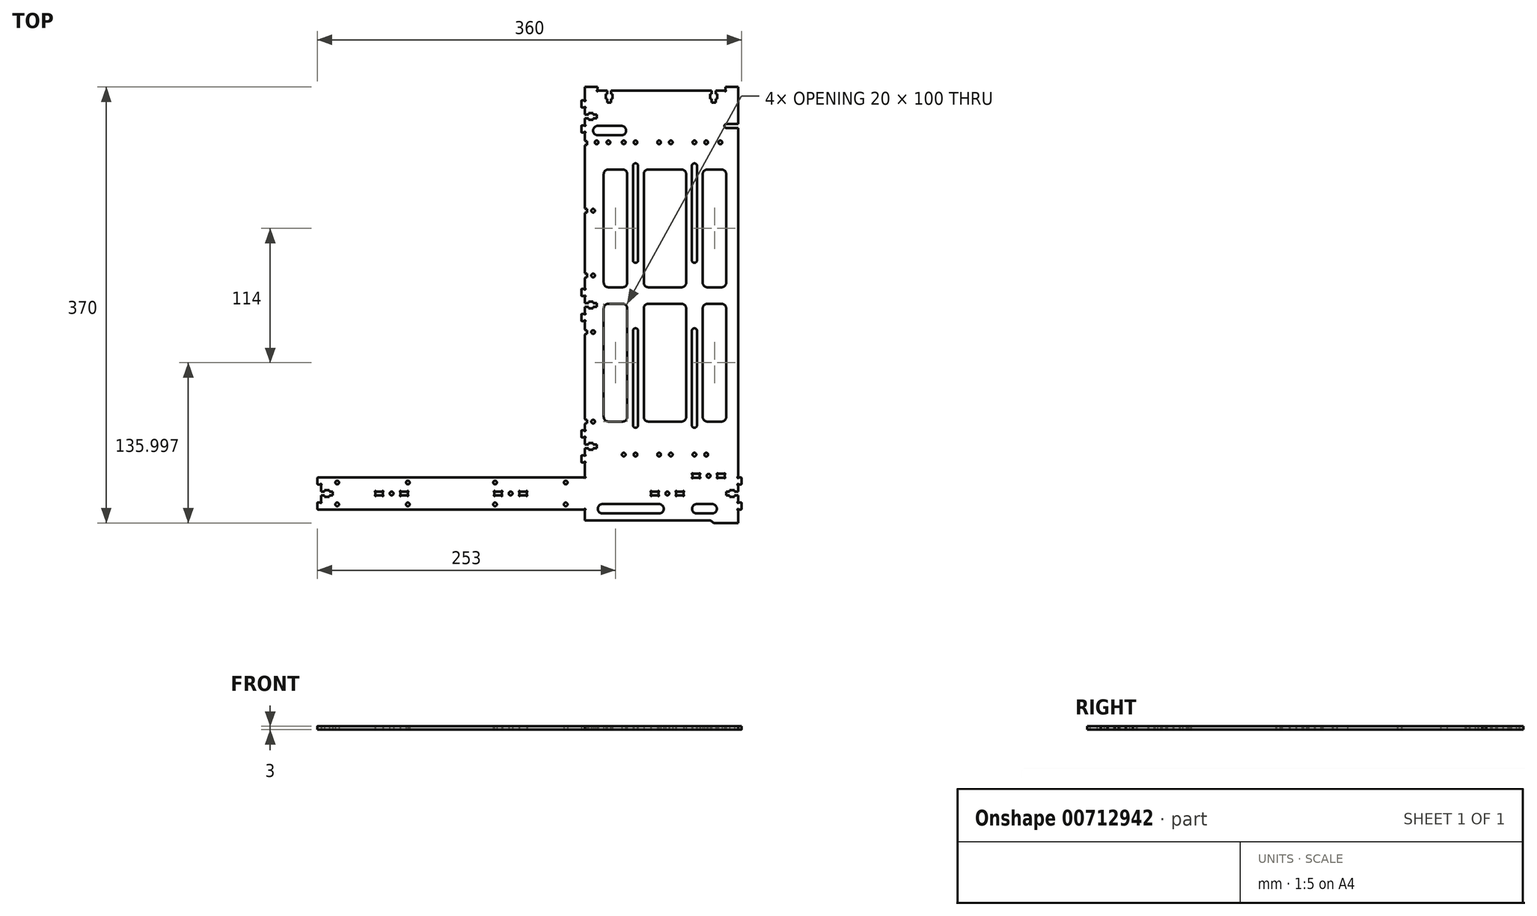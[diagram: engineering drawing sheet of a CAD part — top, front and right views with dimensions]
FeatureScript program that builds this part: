
annotation { "Feature Type Name" : "Feature", "Feature Type Description" : "" }
export const myFeature = defineFeature(function(context is Context, id is Id, definition is map)
    precondition{}
    {
        {
            var Q0;
            Q0=qCreatedBy(makeId("Top.planeOp"),FACE);
            var sketch = newSketch(context, id + "F0", { "sketchPlane" : qUnion([Q0])});
            skCircle(sketch, "E0", {"center": v(30.75, -146.86) * mm, "radius": 1.55 * mm});
            skCircle(sketch, "E1", {"center": v(-103.25, -146.86) * mm, "radius": 1.55 * mm});
            skCircle(sketch, "E2", {"center": v(30.75, -165.45) * mm, "radius": 1.55 * mm});
            skCircle(sketch, "E3", {"center": v(-163.25, -165.45) * mm, "radius": 1.55 * mm});
            skLineSegment(sketch, "E4", {"start": v(-103.3, -156.94) * mm, "end": v(-103.3, -155.37) * mm});
            skArc(sketch, "E5", {"start": v(-103.3, -156.94) * mm, "mid": v(-103.23, -157.19) * mm, "end": v(-103.05, -157.37) * mm});
            skArc(sketch, "E6", {"start": v(-103.73, -158.05) * mm, "mid": v(-102.95, -158.16) * mm, "end": v(-103.05, -157.37) * mm});
            skArc(sketch, "E7", {"start": v(-103.73, -158.05) * mm, "mid": v(-103.92, -157.87) * mm, "end": v(-104.17, -157.8) * mm});
            skLineSegment(sketch, "E8", {"start": v(-108.63, -157.8) * mm, "end": v(-104.17, -157.8) * mm});
            skArc(sketch, "E9", {"start": v(-108.63, -157.8) * mm, "mid": v(-108.88, -157.87) * mm, "end": v(-109.07, -158.05) * mm});
            skArc(sketch, "E10", {"start": v(-109.75, -157.37) * mm, "mid": v(-109.85, -158.16) * mm, "end": v(-109.07, -158.05) * mm});
            skArc(sketch, "E11", {"start": v(-109.75, -157.37) * mm, "mid": v(-109.57, -157.19) * mm, "end": v(-109.5, -156.94) * mm});
            skLineSegment(sketch, "E12", {"start": v(-109.5, -155.37) * mm, "end": v(-109.5, -156.94) * mm});
            skArc(sketch, "E13", {"start": v(-109.5, -155.37) * mm, "mid": v(-109.57, -155.12) * mm, "end": v(-109.75, -154.94) * mm});
            skArc(sketch, "E14", {"start": v(-109.07, -154.25) * mm, "mid": v(-109.85, -154.15) * mm, "end": v(-109.75, -154.94) * mm});
            skArc(sketch, "E15", {"start": v(-109.07, -154.25) * mm, "mid": v(-108.88, -154.44) * mm, "end": v(-108.63, -154.5) * mm});
            skLineSegment(sketch, "E16", {"start": v(-104.17, -154.5) * mm, "end": v(-108.63, -154.5) * mm});
            skArc(sketch, "E17", {"start": v(-104.17, -154.5) * mm, "mid": v(-103.92, -154.44) * mm, "end": v(-103.73, -154.25) * mm});
            skArc(sketch, "E18", {"start": v(-103.05, -154.94) * mm, "mid": v(-102.95, -154.15) * mm, "end": v(-103.73, -154.25) * mm});
            skArc(sketch, "E19", {"start": v(-103.05, -154.94) * mm, "mid": v(-103.23, -155.12) * mm, "end": v(-103.3, -155.37) * mm});
            skLineSegment(sketch, "E20", {"start": v(-124.5, -156.94) * mm, "end": v(-124.5, -155.37) * mm});
            skArc(sketch, "E21", {"start": v(-124.5, -156.94) * mm, "mid": v(-124.43, -157.19) * mm, "end": v(-124.25, -157.37) * mm});
            skArc(sketch, "E22", {"start": v(-124.93, -158.05) * mm, "mid": v(-124.15, -158.16) * mm, "end": v(-124.25, -157.37) * mm});
            skArc(sketch, "E23", {"start": v(-124.93, -158.05) * mm, "mid": v(-125.12, -157.87) * mm, "end": v(-125.37, -157.8) * mm});
            skLineSegment(sketch, "E24", {"start": v(-129.83, -157.8) * mm, "end": v(-125.37, -157.8) * mm});
            skArc(sketch, "E25", {"start": v(-129.83, -157.8) * mm, "mid": v(-130.08, -157.87) * mm, "end": v(-130.27, -158.05) * mm});
            skArc(sketch, "E26", {"start": v(-130.95, -157.37) * mm, "mid": v(-131.05, -158.16) * mm, "end": v(-130.27, -158.05) * mm});
            skArc(sketch, "E27", {"start": v(-130.95, -157.37) * mm, "mid": v(-130.77, -157.19) * mm, "end": v(-130.7, -156.94) * mm});
            skLineSegment(sketch, "E28", {"start": v(-130.7, -155.37) * mm, "end": v(-130.7, -156.94) * mm});
            skArc(sketch, "E29", {"start": v(-130.7, -155.37) * mm, "mid": v(-130.77, -155.12) * mm, "end": v(-130.95, -154.94) * mm});
            skArc(sketch, "E30", {"start": v(-130.27, -154.25) * mm, "mid": v(-131.05, -154.15) * mm, "end": v(-130.95, -154.94) * mm});
            skArc(sketch, "E31", {"start": v(-130.27, -154.25) * mm, "mid": v(-130.08, -154.44) * mm, "end": v(-129.83, -154.5) * mm});
            skLineSegment(sketch, "E32", {"start": v(-125.37, -154.5) * mm, "end": v(-129.83, -154.5) * mm});
            skArc(sketch, "E33", {"start": v(-125.37, -154.5) * mm, "mid": v(-125.12, -154.44) * mm, "end": v(-124.93, -154.25) * mm});
            skArc(sketch, "E34", {"start": v(-124.25, -154.94) * mm, "mid": v(-124.15, -154.15) * mm, "end": v(-124.93, -154.25) * mm});
            skArc(sketch, "E35", {"start": v(-124.25, -154.94) * mm, "mid": v(-124.43, -155.12) * mm, "end": v(-124.5, -155.37) * mm});
            skLineSegment(sketch, "E36", {"start": v(87.8, -18.15) * mm, "end": v(87.8, -98.15) * mm});
            skArc(sketch, "E37", {"start": v(92.2, -18.15) * mm, "mid": v(90, -15.95) * mm, "end": v(87.8, -18.15) * mm});
            skLineSegment(sketch, "E38", {"start": v(92.2, -98.15) * mm, "end": v(92.2, -18.15) * mm});
            skArc(sketch, "E39", {"start": v(87.8, -98.15) * mm, "mid": v(90, -100.35) * mm, "end": v(92.2, -98.15) * mm});
            skLineSegment(sketch, "E40", {"start": v(137.8, -18.15) * mm, "end": v(137.8, -98.15) * mm});
            skArc(sketch, "E41", {"start": v(142.2, -18.15) * mm, "mid": v(140, -15.95) * mm, "end": v(137.8, -18.15) * mm});
            skLineSegment(sketch, "E42", {"start": v(142.2, -98.15) * mm, "end": v(142.2, -18.15) * mm});
            skArc(sketch, "E43", {"start": v(137.8, -98.15) * mm, "mid": v(140, -100.35) * mm, "end": v(142.2, -98.15) * mm});
            skCircle(sketch, "E44", {"center": v(162, 141.85) * mm, "radius": 1.55 * mm});
            skCircle(sketch, "E45", {"center": v(140, 141.85) * mm, "radius": 1.55 * mm});
            skCircle(sketch, "E46", {"center": v(110, 141.85) * mm, "radius": 1.55 * mm});
            skCircle(sketch, "E47", {"center": v(80, 141.85) * mm, "radius": 1.55 * mm});
            skCircle(sketch, "E48", {"center": v(57, 141.85) * mm, "radius": 1.55 * mm});
            skLineSegment(sketch, "E49", {"start": v(165.7, -141.94) * mm, "end": v(165.7, -140.37) * mm});
            skArc(sketch, "E50", {"start": v(165.7, -141.94) * mm, "mid": v(165.77, -142.19) * mm, "end": v(165.95, -142.37) * mm});
            skArc(sketch, "E51", {"start": v(165.27, -143.05) * mm, "mid": v(166.05, -143.16) * mm, "end": v(165.95, -142.37) * mm});
            skArc(sketch, "E52", {"start": v(165.27, -143.05) * mm, "mid": v(165.08, -142.87) * mm, "end": v(164.83, -142.8) * mm});
            skLineSegment(sketch, "E53", {"start": v(160.37, -142.8) * mm, "end": v(164.83, -142.8) * mm});
            skArc(sketch, "E54", {"start": v(160.37, -142.8) * mm, "mid": v(160.12, -142.87) * mm, "end": v(159.93, -143.05) * mm});
            skArc(sketch, "E55", {"start": v(159.25, -142.37) * mm, "mid": v(159.15, -143.16) * mm, "end": v(159.93, -143.05) * mm});
            skArc(sketch, "E56", {"start": v(159.25, -142.37) * mm, "mid": v(159.43, -142.19) * mm, "end": v(159.5, -141.94) * mm});
            skLineSegment(sketch, "E57", {"start": v(159.5, -140.37) * mm, "end": v(159.5, -141.94) * mm});
            skArc(sketch, "E58", {"start": v(159.5, -140.37) * mm, "mid": v(159.43, -140.12) * mm, "end": v(159.25, -139.94) * mm});
            skArc(sketch, "E59", {"start": v(159.93, -139.25) * mm, "mid": v(159.15, -139.15) * mm, "end": v(159.25, -139.94) * mm});
            skArc(sketch, "E60", {"start": v(159.93, -139.25) * mm, "mid": v(160.12, -139.44) * mm, "end": v(160.37, -139.5) * mm});
            skLineSegment(sketch, "E61", {"start": v(164.83, -139.5) * mm, "end": v(160.37, -139.5) * mm});
            skArc(sketch, "E62", {"start": v(164.83, -139.5) * mm, "mid": v(165.08, -139.44) * mm, "end": v(165.27, -139.25) * mm});
            skArc(sketch, "E63", {"start": v(165.95, -139.94) * mm, "mid": v(166.05, -139.15) * mm, "end": v(165.27, -139.25) * mm});
            skArc(sketch, "E64", {"start": v(165.95, -139.94) * mm, "mid": v(165.77, -140.12) * mm, "end": v(165.7, -140.37) * mm});
            skLineSegment(sketch, "E65", {"start": v(144.5, -141.94) * mm, "end": v(144.5, -140.37) * mm});
            skArc(sketch, "E66", {"start": v(144.5, -141.94) * mm, "mid": v(144.57, -142.19) * mm, "end": v(144.75, -142.37) * mm});
            skArc(sketch, "E67", {"start": v(144.07, -143.05) * mm, "mid": v(144.85, -143.16) * mm, "end": v(144.75, -142.37) * mm});
            skArc(sketch, "E68", {"start": v(144.07, -143.05) * mm, "mid": v(143.88, -142.87) * mm, "end": v(143.63, -142.8) * mm});
            skLineSegment(sketch, "E69", {"start": v(139.17, -142.8) * mm, "end": v(143.63, -142.8) * mm});
            skArc(sketch, "E70", {"start": v(139.17, -142.8) * mm, "mid": v(138.92, -142.87) * mm, "end": v(138.73, -143.05) * mm});
            skArc(sketch, "E71", {"start": v(138.05, -142.37) * mm, "mid": v(137.95, -143.16) * mm, "end": v(138.73, -143.05) * mm});
            skArc(sketch, "E72", {"start": v(138.05, -142.37) * mm, "mid": v(138.23, -142.19) * mm, "end": v(138.3, -141.94) * mm});
            skLineSegment(sketch, "E73", {"start": v(138.3, -140.37) * mm, "end": v(138.3, -141.94) * mm});
            skArc(sketch, "E74", {"start": v(138.3, -140.37) * mm, "mid": v(138.23, -140.12) * mm, "end": v(138.05, -139.94) * mm});
            skArc(sketch, "E75", {"start": v(138.73, -139.25) * mm, "mid": v(137.95, -139.15) * mm, "end": v(138.05, -139.94) * mm});
            skArc(sketch, "E76", {"start": v(138.73, -139.25) * mm, "mid": v(138.92, -139.44) * mm, "end": v(139.17, -139.5) * mm});
            skLineSegment(sketch, "E77", {"start": v(143.63, -139.5) * mm, "end": v(139.17, -139.5) * mm});
            skArc(sketch, "E78", {"start": v(143.63, -139.5) * mm, "mid": v(143.88, -139.44) * mm, "end": v(144.07, -139.25) * mm});
            skArc(sketch, "E79", {"start": v(144.75, -139.94) * mm, "mid": v(144.85, -139.15) * mm, "end": v(144.07, -139.25) * mm});
            skArc(sketch, "E80", {"start": v(144.75, -139.94) * mm, "mid": v(144.57, -140.12) * mm, "end": v(144.5, -140.37) * mm});
            skCircle(sketch, "E81", {"center": v(117, -156.15) * mm, "radius": 1.6 * mm});
            skCircle(sketch, "E82", {"center": v(80, -123.15) * mm, "radius": 1.55 * mm});
            skCircle(sketch, "E83", {"center": v(140, -123.15) * mm, "radius": 1.55 * mm});
            skCircle(sketch, "E84", {"center": v(110, -123.15) * mm, "radius": 1.55 * mm});
            skCircle(sketch, "E85", {"center": v(54, -95.15) * mm, "radius": 1.55 * mm});
            skCircle(sketch, "E86", {"center": v(54, 28.85) * mm, "radius": 1.55 * mm});
            skLineSegment(sketch, "E87", {"start": v(-2.3, -156.94) * mm, "end": v(-2.3, -155.37) * mm});
            skArc(sketch, "E88", {"start": v(-2.3, -156.94) * mm, "mid": v(-2.23, -157.19) * mm, "end": v(-2.05, -157.37) * mm});
            skArc(sketch, "E89", {"start": v(-2.73, -158.05) * mm, "mid": v(-1.95, -158.16) * mm, "end": v(-2.05, -157.37) * mm});
            skArc(sketch, "E90", {"start": v(-2.73, -158.05) * mm, "mid": v(-2.92, -157.87) * mm, "end": v(-3.17, -157.8) * mm});
            skLineSegment(sketch, "E91", {"start": v(-7.63, -157.8) * mm, "end": v(-3.17, -157.8) * mm});
            skArc(sketch, "E92", {"start": v(-7.63, -157.8) * mm, "mid": v(-7.88, -157.87) * mm, "end": v(-8.07, -158.05) * mm});
            skArc(sketch, "E93", {"start": v(-8.75, -157.37) * mm, "mid": v(-8.85, -158.16) * mm, "end": v(-8.07, -158.05) * mm});
            skArc(sketch, "E94", {"start": v(-8.75, -157.37) * mm, "mid": v(-8.57, -157.19) * mm, "end": v(-8.5, -156.94) * mm});
            skLineSegment(sketch, "E95", {"start": v(-8.5, -155.37) * mm, "end": v(-8.5, -156.94) * mm});
            skArc(sketch, "E96", {"start": v(-8.5, -155.37) * mm, "mid": v(-8.57, -155.12) * mm, "end": v(-8.75, -154.94) * mm});
            skArc(sketch, "E97", {"start": v(-8.07, -154.25) * mm, "mid": v(-8.85, -154.15) * mm, "end": v(-8.75, -154.94) * mm});
            skArc(sketch, "E98", {"start": v(-8.07, -154.25) * mm, "mid": v(-7.88, -154.44) * mm, "end": v(-7.63, -154.5) * mm});
            skLineSegment(sketch, "E99", {"start": v(-3.17, -154.5) * mm, "end": v(-7.63, -154.5) * mm});
            skArc(sketch, "E100", {"start": v(-3.17, -154.5) * mm, "mid": v(-2.92, -154.44) * mm, "end": v(-2.73, -154.25) * mm});
            skArc(sketch, "E101", {"start": v(-2.05, -154.94) * mm, "mid": v(-1.95, -154.15) * mm, "end": v(-2.73, -154.25) * mm});
            skArc(sketch, "E102", {"start": v(-2.05, -154.94) * mm, "mid": v(-2.23, -155.12) * mm, "end": v(-2.3, -155.37) * mm});
            skLineSegment(sketch, "E103", {"start": v(-23.5, -156.94) * mm, "end": v(-23.5, -155.37) * mm});
            skArc(sketch, "E104", {"start": v(-23.5, -156.94) * mm, "mid": v(-23.43, -157.19) * mm, "end": v(-23.25, -157.37) * mm});
            skArc(sketch, "E105", {"start": v(-23.93, -158.05) * mm, "mid": v(-23.15, -158.16) * mm, "end": v(-23.25, -157.37) * mm});
            skArc(sketch, "E106", {"start": v(-23.93, -158.05) * mm, "mid": v(-24.12, -157.87) * mm, "end": v(-24.37, -157.8) * mm});
            skLineSegment(sketch, "E107", {"start": v(-28.83, -157.8) * mm, "end": v(-24.37, -157.8) * mm});
            skArc(sketch, "E108", {"start": v(-28.83, -157.8) * mm, "mid": v(-29.08, -157.87) * mm, "end": v(-29.27, -158.05) * mm});
            skArc(sketch, "E109", {"start": v(-29.95, -157.37) * mm, "mid": v(-30.05, -158.16) * mm, "end": v(-29.27, -158.05) * mm});
            skArc(sketch, "E110", {"start": v(-29.95, -157.37) * mm, "mid": v(-29.77, -157.19) * mm, "end": v(-29.7, -156.94) * mm});
            skLineSegment(sketch, "E111", {"start": v(-29.7, -155.37) * mm, "end": v(-29.7, -156.94) * mm});
            skArc(sketch, "E112", {"start": v(-29.7, -155.37) * mm, "mid": v(-29.77, -155.12) * mm, "end": v(-29.95, -154.94) * mm});
            skArc(sketch, "E113", {"start": v(-29.27, -154.25) * mm, "mid": v(-30.05, -154.15) * mm, "end": v(-29.95, -154.94) * mm});
            skArc(sketch, "E114", {"start": v(-29.27, -154.25) * mm, "mid": v(-29.08, -154.44) * mm, "end": v(-28.83, -154.5) * mm});
            skLineSegment(sketch, "E115", {"start": v(-24.37, -154.5) * mm, "end": v(-28.83, -154.5) * mm});
            skArc(sketch, "E116", {"start": v(-24.37, -154.5) * mm, "mid": v(-24.12, -154.44) * mm, "end": v(-23.93, -154.25) * mm});
            skArc(sketch, "E117", {"start": v(-23.25, -154.94) * mm, "mid": v(-23.15, -154.15) * mm, "end": v(-23.93, -154.25) * mm});
            skArc(sketch, "E118", {"start": v(-23.25, -154.94) * mm, "mid": v(-23.43, -155.12) * mm, "end": v(-23.5, -155.37) * mm});
            skLineSegment(sketch, "E119", {"start": v(62, -173.15) * mm, "end": v(110, -173.15) * mm});
            skArc(sketch, "E120", {"start": v(62, -165.15) * mm, "mid": v(58, -169.15) * mm, "end": v(62, -173.15) * mm});
            skLineSegment(sketch, "E121", {"start": v(110, -165.15) * mm, "end": v(62, -165.15) * mm});
            skArc(sketch, "E122", {"start": v(110, -173.15) * mm, "mid": v(114, -169.15) * mm, "end": v(110, -165.15) * mm});
            skArc(sketch, "E123", {"start": v(47.25, -170.19) * mm, "mid": v(47.35, -169.4) * mm, "end": v(46.57, -169.5) * mm});
            skArc(sketch, "E124", {"start": v(47.25, -170.19) * mm, "mid": v(47.07, -170.37) * mm, "end": v(47, -170.62) * mm});
            skLineSegment(sketch, "E125", {"start": v(47, -170.62) * mm, "end": v(47, -179.15) * mm});
            skLineSegment(sketch, "E126", {"start": v(47, -179.15) * mm, "end": v(153.17, -179.15) * mm});
            skArc(sketch, "E127", {"start": v(154.59, -179.74) * mm, "mid": v(153.94, -179.3) * mm, "end": v(153.17, -179.15) * mm});
            skLineSegment(sketch, "E128", {"start": v(154.59, -179.74) * mm, "end": v(155.41, -180.57) * mm});
            skArc(sketch, "E129", {"start": v(155.41, -180.57) * mm, "mid": v(156.06, -181) * mm, "end": v(156.83, -181.15) * mm});
            skLineSegment(sketch, "E130", {"start": v(156.83, -181.15) * mm, "end": v(177, -181.15) * mm});
            skLineSegment(sketch, "E131", {"start": v(177, -181.15) * mm, "end": v(177, -170.62) * mm});
            skArc(sketch, "E132", {"start": v(177, -170.62) * mm, "mid": v(176.93, -170.37) * mm, "end": v(176.75, -170.19) * mm});
            skArc(sketch, "E133", {"start": v(177.43, -169.5) * mm, "mid": v(176.65, -169.4) * mm, "end": v(176.75, -170.19) * mm});
            skArc(sketch, "E134", {"start": v(177.43, -169.5) * mm, "mid": v(177.62, -169.69) * mm, "end": v(177.87, -169.75) * mm});
            skLineSegment(sketch, "E135", {"start": v(177.87, -169.75) * mm, "end": v(179.5, -169.75) * mm});
            skArc(sketch, "E136", {"start": v(179.5, -169.75) * mm, "mid": v(179.85, -169.6) * mm, "end": v(180, -169.25) * mm});
            skLineSegment(sketch, "E137", {"start": v(180, -169.25) * mm, "end": v(180, -164.25) * mm});
            skArc(sketch, "E138", {"start": v(180, -164.25) * mm, "mid": v(179.85, -163.9) * mm, "end": v(179.5, -163.75) * mm});
            skLineSegment(sketch, "E139", {"start": v(179.5, -163.75) * mm, "end": v(177.87, -163.75) * mm});
            skArc(sketch, "E140", {"start": v(177.87, -163.75) * mm, "mid": v(177.62, -163.82) * mm, "end": v(177.43, -164) * mm});
            skArc(sketch, "E141", {"start": v(176.75, -163.32) * mm, "mid": v(176.65, -164.1) * mm, "end": v(177.43, -164) * mm});
            skArc(sketch, "E142", {"start": v(176.75, -163.32) * mm, "mid": v(176.93, -163.14) * mm, "end": v(177, -162.89) * mm});
            skLineSegment(sketch, "E143", {"start": v(177, -162.89) * mm, "end": v(177, -157.75) * mm});
            skLineSegment(sketch, "E144", {"start": v(177, -157.75) * mm, "end": v(174, -157.75) * mm});
            skLineSegment(sketch, "E145", {"start": v(174, -157.75) * mm, "end": v(174, -159.03) * mm});
            skLineSegment(sketch, "E146", {"start": v(174, -159.03) * mm, "end": v(170, -159.03) * mm});
            skLineSegment(sketch, "E147", {"start": v(170, -159.03) * mm, "end": v(170, -157.75) * mm});
            skLineSegment(sketch, "E148", {"start": v(170, -157.75) * mm, "end": v(167, -157.75) * mm});
            skLineSegment(sketch, "E149", {"start": v(167, -157.75) * mm, "end": v(167, -154.55) * mm});
            skLineSegment(sketch, "E150", {"start": v(167, -154.55) * mm, "end": v(170, -154.55) * mm});
            skLineSegment(sketch, "E151", {"start": v(170, -154.55) * mm, "end": v(170, -153.28) * mm});
            skLineSegment(sketch, "E152", {"start": v(170, -153.28) * mm, "end": v(174, -153.28) * mm});
            skLineSegment(sketch, "E153", {"start": v(174, -153.28) * mm, "end": v(174, -154.55) * mm});
            skLineSegment(sketch, "E154", {"start": v(174, -154.55) * mm, "end": v(177, -154.55) * mm});
            skLineSegment(sketch, "E155", {"start": v(177, -154.55) * mm, "end": v(177, -149.42) * mm});
            skArc(sketch, "E156", {"start": v(177, -149.42) * mm, "mid": v(176.93, -149.17) * mm, "end": v(176.75, -148.99) * mm});
            skArc(sketch, "E157", {"start": v(177.43, -148.3) * mm, "mid": v(176.65, -148.2) * mm, "end": v(176.75, -148.99) * mm});
            skArc(sketch, "E158", {"start": v(177.43, -148.3) * mm, "mid": v(177.62, -148.49) * mm, "end": v(177.87, -148.55) * mm});
            skLineSegment(sketch, "E159", {"start": v(177.87, -148.55) * mm, "end": v(179.5, -148.55) * mm});
            skArc(sketch, "E160", {"start": v(179.5, -148.55) * mm, "mid": v(179.85, -148.4) * mm, "end": v(180, -148.05) * mm});
            skLineSegment(sketch, "E161", {"start": v(180, -148.05) * mm, "end": v(180, -143.05) * mm});
            skArc(sketch, "E162", {"start": v(180, -143.05) * mm, "mid": v(179.85, -142.7) * mm, "end": v(179.5, -142.55) * mm});
            skLineSegment(sketch, "E163", {"start": v(179.5, -142.55) * mm, "end": v(177.87, -142.55) * mm});
            skArc(sketch, "E164", {"start": v(177.87, -142.55) * mm, "mid": v(177.62, -142.62) * mm, "end": v(177.43, -142.8) * mm});
            skArc(sketch, "E165", {"start": v(176.75, -142.12) * mm, "mid": v(176.65, -142.9) * mm, "end": v(177.43, -142.8) * mm});
            skArc(sketch, "E166", {"start": v(176.75, -142.12) * mm, "mid": v(176.93, -141.94) * mm, "end": v(177, -141.69) * mm});
            skLineSegment(sketch, "E167", {"start": v(177, -141.69) * mm, "end": v(177, 153.9) * mm});
            skLineSegment(sketch, "E168", {"start": v(177, 153.9) * mm, "end": v(176.75, 154.15) * mm});
            skLineSegment(sketch, "E169", {"start": v(176.75, 154.15) * mm, "end": v(167, 154.15) * mm});
            skArc(sketch, "E170", {"start": v(167, 157.35) * mm, "mid": v(165.4, 155.75) * mm, "end": v(167, 154.15) * mm});
            skLineSegment(sketch, "E171", {"start": v(167, 157.35) * mm, "end": v(176.75, 157.35) * mm});
            skLineSegment(sketch, "E172", {"start": v(176.75, 157.35) * mm, "end": v(177, 157.6) * mm});
            skLineSegment(sketch, "E173", {"start": v(177, 157.6) * mm, "end": v(177, 188.85) * mm});
            skLineSegment(sketch, "E174", {"start": v(177, 188.85) * mm, "end": v(166.35, 188.85) * mm});
            skLineSegment(sketch, "E175", {"start": v(166.35, 188.85) * mm, "end": v(166.35, 186.61) * mm});
            skArc(sketch, "E176", {"start": v(166.35, 186.61) * mm, "mid": v(166.42, 186.36) * mm, "end": v(166.6, 186.18) * mm});
            skArc(sketch, "E177", {"start": v(165.92, 185.5) * mm, "mid": v(166.7, 185.4) * mm, "end": v(166.6, 186.18) * mm});
            skArc(sketch, "E178", {"start": v(165.92, 185.5) * mm, "mid": v(165.73, 185.68) * mm, "end": v(165.48, 185.75) * mm});
            skLineSegment(sketch, "E179", {"start": v(165.48, 185.75) * mm, "end": v(157.95, 185.75) * mm});
            skLineSegment(sketch, "E180", {"start": v(157.95, 185.75) * mm, "end": v(157.95, 182.75) * mm});
            skLineSegment(sketch, "E181", {"start": v(157.95, 182.75) * mm, "end": v(159.22, 182.75) * mm});
            skLineSegment(sketch, "E182", {"start": v(159.22, 182.75) * mm, "end": v(159.22, 178.75) * mm});
            skLineSegment(sketch, "E183", {"start": v(159.22, 178.75) * mm, "end": v(157.95, 178.75) * mm});
            skLineSegment(sketch, "E184", {"start": v(157.95, 178.75) * mm, "end": v(157.95, 175.75) * mm});
            skLineSegment(sketch, "E185", {"start": v(157.95, 175.75) * mm, "end": v(154.75, 175.75) * mm});
            skLineSegment(sketch, "E186", {"start": v(154.75, 175.75) * mm, "end": v(154.75, 178.75) * mm});
            skLineSegment(sketch, "E187", {"start": v(154.75, 178.75) * mm, "end": v(153.47, 178.75) * mm});
            skLineSegment(sketch, "E188", {"start": v(153.47, 178.75) * mm, "end": v(153.47, 182.75) * mm});
            skLineSegment(sketch, "E189", {"start": v(153.47, 182.75) * mm, "end": v(154.75, 182.75) * mm});
            skLineSegment(sketch, "E190", {"start": v(154.75, 182.75) * mm, "end": v(154.75, 185.75) * mm});
            skLineSegment(sketch, "E191", {"start": v(154.75, 185.75) * mm, "end": v(69.25, 185.75) * mm});
            skLineSegment(sketch, "E192", {"start": v(69.25, 185.75) * mm, "end": v(69.25, 182.75) * mm});
            skLineSegment(sketch, "E193", {"start": v(69.25, 182.75) * mm, "end": v(70.53, 182.75) * mm});
            skLineSegment(sketch, "E194", {"start": v(70.53, 182.75) * mm, "end": v(70.53, 178.75) * mm});
            skLineSegment(sketch, "E195", {"start": v(70.53, 178.75) * mm, "end": v(69.25, 178.75) * mm});
            skLineSegment(sketch, "E196", {"start": v(69.25, 178.75) * mm, "end": v(69.25, 175.75) * mm});
            skLineSegment(sketch, "E197", {"start": v(69.25, 175.75) * mm, "end": v(66.05, 175.75) * mm});
            skLineSegment(sketch, "E198", {"start": v(66.05, 175.75) * mm, "end": v(66.05, 178.75) * mm});
            skLineSegment(sketch, "E199", {"start": v(66.05, 178.75) * mm, "end": v(64.78, 178.75) * mm});
            skLineSegment(sketch, "E200", {"start": v(64.78, 178.75) * mm, "end": v(64.78, 182.75) * mm});
            skLineSegment(sketch, "E201", {"start": v(64.78, 182.75) * mm, "end": v(66.05, 182.75) * mm});
            skLineSegment(sketch, "E202", {"start": v(66.05, 182.75) * mm, "end": v(66.05, 185.75) * mm});
            skLineSegment(sketch, "E203", {"start": v(66.05, 185.75) * mm, "end": v(58.52, 185.75) * mm});
            skArc(sketch, "E204", {"start": v(58.52, 185.75) * mm, "mid": v(58.27, 185.68) * mm, "end": v(58.08, 185.5) * mm});
            skArc(sketch, "E205", {"start": v(57.4, 186.18) * mm, "mid": v(57.3, 185.4) * mm, "end": v(58.08, 185.5) * mm});
            skArc(sketch, "E206", {"start": v(57.4, 186.18) * mm, "mid": v(57.58, 186.36) * mm, "end": v(57.65, 186.61) * mm});
            skLineSegment(sketch, "E207", {"start": v(57.65, 186.61) * mm, "end": v(57.65, 188.85) * mm});
            skLineSegment(sketch, "E208", {"start": v(57.65, 188.85) * mm, "end": v(47, 188.85) * mm});
            skLineSegment(sketch, "E209", {"start": v(47, 188.85) * mm, "end": v(47, 178.31) * mm});
            skArc(sketch, "E210", {"start": v(47, 178.31) * mm, "mid": v(47.07, 178.06) * mm, "end": v(47.25, 177.88) * mm});
            skArc(sketch, "E211", {"start": v(46.57, 177.2) * mm, "mid": v(47.35, 177.1) * mm, "end": v(47.25, 177.88) * mm});
            skArc(sketch, "E212", {"start": v(46.57, 177.2) * mm, "mid": v(46.38, 177.38) * mm, "end": v(46.13, 177.45) * mm});
            skLineSegment(sketch, "E213", {"start": v(46.13, 177.45) * mm, "end": v(44.5, 177.45) * mm});
            skArc(sketch, "E214", {"start": v(44.5, 177.45) * mm, "mid": v(44.15, 177.3) * mm, "end": v(44, 176.95) * mm});
            skLineSegment(sketch, "E215", {"start": v(44, 176.95) * mm, "end": v(44, 171.95) * mm});
            skArc(sketch, "E216", {"start": v(44, 171.95) * mm, "mid": v(44.15, 171.6) * mm, "end": v(44.5, 171.45) * mm});
            skLineSegment(sketch, "E217", {"start": v(44.5, 171.45) * mm, "end": v(46.13, 171.45) * mm});
            skArc(sketch, "E218", {"start": v(46.13, 171.45) * mm, "mid": v(46.38, 171.51) * mm, "end": v(46.57, 171.7) * mm});
            skArc(sketch, "E219", {"start": v(47.25, 171.01) * mm, "mid": v(47.35, 171.8) * mm, "end": v(46.57, 171.7) * mm});
            skArc(sketch, "E220", {"start": v(47.25, 171.01) * mm, "mid": v(47.07, 170.83) * mm, "end": v(47, 170.58) * mm});
            skLineSegment(sketch, "E221", {"start": v(47, 170.58) * mm, "end": v(47, 165.45) * mm});
            skLineSegment(sketch, "E222", {"start": v(47, 165.45) * mm, "end": v(50, 165.45) * mm});
            skLineSegment(sketch, "E223", {"start": v(50, 165.45) * mm, "end": v(50, 166.72) * mm});
            skLineSegment(sketch, "E224", {"start": v(50, 166.72) * mm, "end": v(54, 166.72) * mm});
            skLineSegment(sketch, "E225", {"start": v(54, 166.72) * mm, "end": v(54, 165.45) * mm});
            skLineSegment(sketch, "E226", {"start": v(54, 165.45) * mm, "end": v(57, 165.45) * mm});
            skLineSegment(sketch, "E227", {"start": v(57, 165.45) * mm, "end": v(57, 162.25) * mm});
            skLineSegment(sketch, "E228", {"start": v(57, 162.25) * mm, "end": v(54, 162.25) * mm});
            skLineSegment(sketch, "E229", {"start": v(54, 162.25) * mm, "end": v(54, 160.97) * mm});
            skLineSegment(sketch, "E230", {"start": v(54, 160.97) * mm, "end": v(50, 160.97) * mm});
            skLineSegment(sketch, "E231", {"start": v(50, 160.97) * mm, "end": v(50, 162.25) * mm});
            skLineSegment(sketch, "E232", {"start": v(50, 162.25) * mm, "end": v(47, 162.25) * mm});
            skLineSegment(sketch, "E233", {"start": v(47, 162.25) * mm, "end": v(47, 157.11) * mm});
            skArc(sketch, "E234", {"start": v(47, 157.11) * mm, "mid": v(47.07, 156.86) * mm, "end": v(47.25, 156.68) * mm});
            skArc(sketch, "E235", {"start": v(46.57, 156) * mm, "mid": v(47.35, 155.9) * mm, "end": v(47.25, 156.68) * mm});
            skArc(sketch, "E236", {"start": v(46.57, 156) * mm, "mid": v(46.38, 156.18) * mm, "end": v(46.13, 156.25) * mm});
            skLineSegment(sketch, "E237", {"start": v(46.13, 156.25) * mm, "end": v(44.5, 156.25) * mm});
            skArc(sketch, "E238", {"start": v(44.5, 156.25) * mm, "mid": v(44.15, 156.1) * mm, "end": v(44, 155.75) * mm});
            skLineSegment(sketch, "E239", {"start": v(44, 155.75) * mm, "end": v(44, 150.75) * mm});
            skArc(sketch, "E240", {"start": v(44, 150.75) * mm, "mid": v(44.15, 150.4) * mm, "end": v(44.5, 150.25) * mm});
            skLineSegment(sketch, "E241", {"start": v(44.5, 150.25) * mm, "end": v(46.13, 150.25) * mm});
            skArc(sketch, "E242", {"start": v(46.13, 150.25) * mm, "mid": v(46.38, 150.31) * mm, "end": v(46.57, 150.5) * mm});
            skArc(sketch, "E243", {"start": v(47.25, 149.81) * mm, "mid": v(47.35, 150.6) * mm, "end": v(46.57, 150.5) * mm});
            skArc(sketch, "E244", {"start": v(47.25, 149.81) * mm, "mid": v(47.07, 149.63) * mm, "end": v(47, 149.38) * mm});
            skLineSegment(sketch, "E245", {"start": v(47, 149.38) * mm, "end": v(47, 143.35) * mm});
            skLineSegment(sketch, "E246", {"start": v(47, 143.35) * mm, "end": v(47.5, 142.85) * mm});
            skLineSegment(sketch, "E247", {"start": v(47.5, 142.85) * mm, "end": v(49, 142.85) * mm});
            skLineSegment(sketch, "E248", {"start": v(49, 142.85) * mm, "end": v(49, 139.85) * mm});
            skLineSegment(sketch, "E249", {"start": v(49, 139.85) * mm, "end": v(47.5, 139.85) * mm});
            skLineSegment(sketch, "E250", {"start": v(47.5, 139.85) * mm, "end": v(47, 139.35) * mm});
            skLineSegment(sketch, "E251", {"start": v(47, 139.35) * mm, "end": v(47, 85.85) * mm});
            skLineSegment(sketch, "E252", {"start": v(47, 85.85) * mm, "end": v(47.5, 85.35) * mm});
            skLineSegment(sketch, "E253", {"start": v(47.5, 85.35) * mm, "end": v(49, 85.35) * mm});
            skLineSegment(sketch, "E254", {"start": v(49, 85.35) * mm, "end": v(49, 82.35) * mm});
            skLineSegment(sketch, "E255", {"start": v(49, 82.35) * mm, "end": v(47.5, 82.35) * mm});
            skLineSegment(sketch, "E256", {"start": v(47.5, 82.35) * mm, "end": v(47, 81.85) * mm});
            skLineSegment(sketch, "E257", {"start": v(47, 81.85) * mm, "end": v(47, 30.85) * mm});
            skLineSegment(sketch, "E258", {"start": v(47, 30.85) * mm, "end": v(47.5, 30.35) * mm});
            skLineSegment(sketch, "E259", {"start": v(47.5, 30.35) * mm, "end": v(49, 30.35) * mm});
            skLineSegment(sketch, "E260", {"start": v(49, 30.35) * mm, "end": v(49, 27.35) * mm});
            skLineSegment(sketch, "E261", {"start": v(49, 27.35) * mm, "end": v(47.5, 27.35) * mm});
            skLineSegment(sketch, "E262", {"start": v(47.5, 27.35) * mm, "end": v(47, 26.85) * mm});
            skLineSegment(sketch, "E263", {"start": v(47, 26.85) * mm, "end": v(47, 18.31) * mm});
            skArc(sketch, "E264", {"start": v(47, 18.31) * mm, "mid": v(47.07, 18.06) * mm, "end": v(47.25, 17.88) * mm});
            skArc(sketch, "E265", {"start": v(46.57, 17.2) * mm, "mid": v(47.35, 17.1) * mm, "end": v(47.25, 17.88) * mm});
            skArc(sketch, "E266", {"start": v(46.57, 17.2) * mm, "mid": v(46.38, 17.38) * mm, "end": v(46.13, 17.45) * mm});
            skLineSegment(sketch, "E267", {"start": v(46.13, 17.45) * mm, "end": v(44.5, 17.45) * mm});
            skArc(sketch, "E268", {"start": v(44.5, 17.45) * mm, "mid": v(44.15, 17.3) * mm, "end": v(44, 16.95) * mm});
            skLineSegment(sketch, "E269", {"start": v(44, 16.95) * mm, "end": v(44, 11.95) * mm});
            skArc(sketch, "E270", {"start": v(44, 11.95) * mm, "mid": v(44.15, 11.6) * mm, "end": v(44.5, 11.45) * mm});
            skLineSegment(sketch, "E271", {"start": v(44.5, 11.45) * mm, "end": v(46.13, 11.45) * mm});
            skArc(sketch, "E272", {"start": v(46.13, 11.45) * mm, "mid": v(46.38, 11.51) * mm, "end": v(46.57, 11.7) * mm});
            skArc(sketch, "E273", {"start": v(47.25, 11.01) * mm, "mid": v(47.35, 11.8) * mm, "end": v(46.57, 11.7) * mm});
            skArc(sketch, "E274", {"start": v(47.25, 11.01) * mm, "mid": v(47.07, 10.83) * mm, "end": v(47, 10.58) * mm});
            skLineSegment(sketch, "E275", {"start": v(47, 10.58) * mm, "end": v(47, 5.45) * mm});
            skLineSegment(sketch, "E276", {"start": v(47, 5.45) * mm, "end": v(50, 5.45) * mm});
            skLineSegment(sketch, "E277", {"start": v(50, 5.45) * mm, "end": v(50, 6.72) * mm});
            skLineSegment(sketch, "E278", {"start": v(50, 6.72) * mm, "end": v(54, 6.72) * mm});
            skLineSegment(sketch, "E279", {"start": v(54, 6.72) * mm, "end": v(54, 5.45) * mm});
            skLineSegment(sketch, "E280", {"start": v(54, 5.45) * mm, "end": v(57, 5.45) * mm});
            skLineSegment(sketch, "E281", {"start": v(57, 5.45) * mm, "end": v(57, 2.25) * mm});
            skLineSegment(sketch, "E282", {"start": v(57, 2.25) * mm, "end": v(54, 2.25) * mm});
            skLineSegment(sketch, "E283", {"start": v(54, 2.25) * mm, "end": v(54, 0.97) * mm});
            skLineSegment(sketch, "E284", {"start": v(54, 0.97) * mm, "end": v(50, 0.97) * mm});
            skLineSegment(sketch, "E285", {"start": v(50, 0.97) * mm, "end": v(50, 2.25) * mm});
            skLineSegment(sketch, "E286", {"start": v(50, 2.25) * mm, "end": v(47, 2.25) * mm});
            skLineSegment(sketch, "E287", {"start": v(47, 2.25) * mm, "end": v(47, -2.89) * mm});
            skArc(sketch, "E288", {"start": v(47, -2.89) * mm, "mid": v(47.07, -3.14) * mm, "end": v(47.25, -3.32) * mm});
            skArc(sketch, "E289", {"start": v(46.57, -4) * mm, "mid": v(47.35, -4.1) * mm, "end": v(47.25, -3.32) * mm});
            skArc(sketch, "E290", {"start": v(46.57, -4) * mm, "mid": v(46.38, -3.82) * mm, "end": v(46.13, -3.75) * mm});
            skLineSegment(sketch, "E291", {"start": v(46.13, -3.75) * mm, "end": v(44.5, -3.75) * mm});
            skArc(sketch, "E292", {"start": v(44.5, -3.75) * mm, "mid": v(44.15, -3.9) * mm, "end": v(44, -4.25) * mm});
            skLineSegment(sketch, "E293", {"start": v(44, -4.25) * mm, "end": v(44, -9.25) * mm});
            skArc(sketch, "E294", {"start": v(44, -9.25) * mm, "mid": v(44.15, -9.6) * mm, "end": v(44.5, -9.75) * mm});
            skLineSegment(sketch, "E295", {"start": v(44.5, -9.75) * mm, "end": v(46.13, -9.75) * mm});
            skArc(sketch, "E296", {"start": v(46.13, -9.75) * mm, "mid": v(46.38, -9.69) * mm, "end": v(46.57, -9.5) * mm});
            skArc(sketch, "E297", {"start": v(47.25, -10.19) * mm, "mid": v(47.35, -9.4) * mm, "end": v(46.57, -9.5) * mm});
            skArc(sketch, "E298", {"start": v(47.25, -10.19) * mm, "mid": v(47.07, -10.37) * mm, "end": v(47, -10.62) * mm});
            skLineSegment(sketch, "E299", {"start": v(47, -10.62) * mm, "end": v(47, -17.15) * mm});
            skLineSegment(sketch, "E300", {"start": v(47, -17.15) * mm, "end": v(47.5, -17.65) * mm});
            skLineSegment(sketch, "E301", {"start": v(47.5, -17.65) * mm, "end": v(49, -17.65) * mm});
            skLineSegment(sketch, "E302", {"start": v(49, -17.65) * mm, "end": v(49, -20.65) * mm});
            skLineSegment(sketch, "E303", {"start": v(49, -20.65) * mm, "end": v(47.5, -20.65) * mm});
            skLineSegment(sketch, "E304", {"start": v(47.5, -20.65) * mm, "end": v(47, -21.15) * mm});
            skLineSegment(sketch, "E305", {"start": v(47, -21.15) * mm, "end": v(47, -93.15) * mm});
            skLineSegment(sketch, "E306", {"start": v(47, -93.15) * mm, "end": v(47.5, -93.65) * mm});
            skLineSegment(sketch, "E307", {"start": v(47.5, -93.65) * mm, "end": v(49, -93.65) * mm});
            skLineSegment(sketch, "E308", {"start": v(49, -93.65) * mm, "end": v(49, -96.65) * mm});
            skLineSegment(sketch, "E309", {"start": v(49, -96.65) * mm, "end": v(47.5, -96.65) * mm});
            skLineSegment(sketch, "E310", {"start": v(47.5, -96.65) * mm, "end": v(47, -97.15) * mm});
            skLineSegment(sketch, "E311", {"start": v(47, -97.15) * mm, "end": v(47, -101.69) * mm});
            skArc(sketch, "E312", {"start": v(47, -101.69) * mm, "mid": v(47.07, -101.94) * mm, "end": v(47.25, -102.12) * mm});
            skArc(sketch, "E313", {"start": v(46.57, -102.8) * mm, "mid": v(47.35, -102.9) * mm, "end": v(47.25, -102.12) * mm});
            skArc(sketch, "E314", {"start": v(46.57, -102.8) * mm, "mid": v(46.38, -102.62) * mm, "end": v(46.13, -102.55) * mm});
            skLineSegment(sketch, "E315", {"start": v(46.13, -102.55) * mm, "end": v(44.5, -102.55) * mm});
            skArc(sketch, "E316", {"start": v(44.5, -102.55) * mm, "mid": v(44.15, -102.7) * mm, "end": v(44, -103.05) * mm});
            skLineSegment(sketch, "E317", {"start": v(44, -103.05) * mm, "end": v(44, -108.05) * mm});
            skArc(sketch, "E318", {"start": v(44, -108.05) * mm, "mid": v(44.15, -108.4) * mm, "end": v(44.5, -108.55) * mm});
            skLineSegment(sketch, "E319", {"start": v(44.5, -108.55) * mm, "end": v(46.13, -108.55) * mm});
            skArc(sketch, "E320", {"start": v(46.13, -108.55) * mm, "mid": v(46.38, -108.49) * mm, "end": v(46.57, -108.3) * mm});
            skArc(sketch, "E321", {"start": v(47.25, -108.99) * mm, "mid": v(47.35, -108.2) * mm, "end": v(46.57, -108.3) * mm});
            skArc(sketch, "E322", {"start": v(47.25, -108.99) * mm, "mid": v(47.07, -109.17) * mm, "end": v(47, -109.42) * mm});
            skLineSegment(sketch, "E323", {"start": v(47, -109.42) * mm, "end": v(47, -114.55) * mm});
            skLineSegment(sketch, "E324", {"start": v(47, -114.55) * mm, "end": v(50, -114.55) * mm});
            skLineSegment(sketch, "E325", {"start": v(50, -114.55) * mm, "end": v(50, -113.28) * mm});
            skLineSegment(sketch, "E326", {"start": v(50, -113.28) * mm, "end": v(54, -113.28) * mm});
            skLineSegment(sketch, "E327", {"start": v(54, -113.28) * mm, "end": v(54, -114.55) * mm});
            skLineSegment(sketch, "E328", {"start": v(54, -114.55) * mm, "end": v(57, -114.55) * mm});
            skLineSegment(sketch, "E329", {"start": v(57, -114.55) * mm, "end": v(57, -117.75) * mm});
            skLineSegment(sketch, "E330", {"start": v(57, -117.75) * mm, "end": v(54, -117.75) * mm});
            skLineSegment(sketch, "E331", {"start": v(54, -117.75) * mm, "end": v(54, -119.03) * mm});
            skLineSegment(sketch, "E332", {"start": v(54, -119.03) * mm, "end": v(50, -119.03) * mm});
            skLineSegment(sketch, "E333", {"start": v(50, -119.03) * mm, "end": v(50, -117.75) * mm});
            skLineSegment(sketch, "E334", {"start": v(50, -117.75) * mm, "end": v(47, -117.75) * mm});
            skLineSegment(sketch, "E335", {"start": v(47, -117.75) * mm, "end": v(47, -122.89) * mm});
            skArc(sketch, "E336", {"start": v(47, -122.89) * mm, "mid": v(47.07, -123.14) * mm, "end": v(47.25, -123.32) * mm});
            skArc(sketch, "E337", {"start": v(46.57, -124) * mm, "mid": v(47.35, -124.1) * mm, "end": v(47.25, -123.32) * mm});
            skArc(sketch, "E338", {"start": v(46.57, -124) * mm, "mid": v(46.38, -123.82) * mm, "end": v(46.13, -123.75) * mm});
            skLineSegment(sketch, "E339", {"start": v(46.13, -123.75) * mm, "end": v(44.5, -123.75) * mm});
            skArc(sketch, "E340", {"start": v(44.5, -123.75) * mm, "mid": v(44.15, -123.9) * mm, "end": v(44, -124.25) * mm});
            skLineSegment(sketch, "E341", {"start": v(44, -124.25) * mm, "end": v(44, -129.25) * mm});
            skArc(sketch, "E342", {"start": v(44, -129.25) * mm, "mid": v(44.15, -129.6) * mm, "end": v(44.5, -129.75) * mm});
            skLineSegment(sketch, "E343", {"start": v(44.5, -129.75) * mm, "end": v(46.13, -129.75) * mm});
            skArc(sketch, "E344", {"start": v(46.13, -129.75) * mm, "mid": v(46.38, -129.69) * mm, "end": v(46.57, -129.5) * mm});
            skArc(sketch, "E345", {"start": v(47.25, -130.19) * mm, "mid": v(47.35, -129.4) * mm, "end": v(46.57, -129.5) * mm});
            skArc(sketch, "E346", {"start": v(47.25, -130.19) * mm, "mid": v(47.07, -130.37) * mm, "end": v(47, -130.62) * mm});
            skLineSegment(sketch, "E347", {"start": v(47, -130.62) * mm, "end": v(47, -141.69) * mm});
            skArc(sketch, "E348", {"start": v(47, -141.69) * mm, "mid": v(47.07, -141.94) * mm, "end": v(47.25, -142.12) * mm});
            skArc(sketch, "E349", {"start": v(46.57, -142.8) * mm, "mid": v(47.35, -142.9) * mm, "end": v(47.25, -142.12) * mm});
            skArc(sketch, "E350", {"start": v(46.57, -142.8) * mm, "mid": v(46.38, -142.62) * mm, "end": v(46.13, -142.55) * mm});
            skLineSegment(sketch, "E351", {"start": v(46.13, -142.55) * mm, "end": v(-179.5, -142.55) * mm});
            skArc(sketch, "E352", {"start": v(-179.5, -142.55) * mm, "mid": v(-179.85, -142.7) * mm, "end": v(-180, -143.05) * mm});
            skLineSegment(sketch, "E353", {"start": v(-180, -143.05) * mm, "end": v(-180, -148.05) * mm});
            skArc(sketch, "E354", {"start": v(-180, -148.05) * mm, "mid": v(-179.85, -148.4) * mm, "end": v(-179.5, -148.55) * mm});
            skLineSegment(sketch, "E355", {"start": v(-179.5, -148.55) * mm, "end": v(-177.87, -148.55) * mm});
            skArc(sketch, "E356", {"start": v(-177.87, -148.55) * mm, "mid": v(-177.62, -148.49) * mm, "end": v(-177.43, -148.3) * mm});
            skArc(sketch, "E357", {"start": v(-176.75, -148.99) * mm, "mid": v(-176.65, -148.2) * mm, "end": v(-177.43, -148.3) * mm});
            skArc(sketch, "E358", {"start": v(-176.75, -148.99) * mm, "mid": v(-176.93, -149.17) * mm, "end": v(-177, -149.42) * mm});
            skLineSegment(sketch, "E359", {"start": v(-177, -149.42) * mm, "end": v(-177, -154.55) * mm});
            skLineSegment(sketch, "E360", {"start": v(-177, -154.55) * mm, "end": v(-174, -154.55) * mm});
            skLineSegment(sketch, "E361", {"start": v(-174, -154.55) * mm, "end": v(-174, -153.28) * mm});
            skLineSegment(sketch, "E362", {"start": v(-174, -153.28) * mm, "end": v(-170, -153.28) * mm});
            skLineSegment(sketch, "E363", {"start": v(-170, -153.28) * mm, "end": v(-170, -154.55) * mm});
            skLineSegment(sketch, "E364", {"start": v(-170, -154.55) * mm, "end": v(-167, -154.55) * mm});
            skLineSegment(sketch, "E365", {"start": v(-167, -154.55) * mm, "end": v(-167, -157.75) * mm});
            skLineSegment(sketch, "E366", {"start": v(-167, -157.75) * mm, "end": v(-170, -157.75) * mm});
            skLineSegment(sketch, "E367", {"start": v(-170, -157.75) * mm, "end": v(-170, -159.03) * mm});
            skLineSegment(sketch, "E368", {"start": v(-170, -159.03) * mm, "end": v(-174, -159.03) * mm});
            skLineSegment(sketch, "E369", {"start": v(-174, -159.03) * mm, "end": v(-174, -157.75) * mm});
            skLineSegment(sketch, "E370", {"start": v(-174, -157.75) * mm, "end": v(-177, -157.75) * mm});
            skLineSegment(sketch, "E371", {"start": v(-177, -157.75) * mm, "end": v(-177, -162.89) * mm});
            skArc(sketch, "E372", {"start": v(-177, -162.89) * mm, "mid": v(-176.93, -163.14) * mm, "end": v(-176.75, -163.32) * mm});
            skArc(sketch, "E373", {"start": v(-177.43, -164) * mm, "mid": v(-176.65, -164.1) * mm, "end": v(-176.75, -163.32) * mm});
            skArc(sketch, "E374", {"start": v(-177.43, -164) * mm, "mid": v(-177.62, -163.82) * mm, "end": v(-177.87, -163.75) * mm});
            skLineSegment(sketch, "E375", {"start": v(-177.87, -163.75) * mm, "end": v(-179.5, -163.75) * mm});
            skArc(sketch, "E376", {"start": v(-179.5, -163.75) * mm, "mid": v(-179.85, -163.9) * mm, "end": v(-180, -164.25) * mm});
            skLineSegment(sketch, "E377", {"start": v(-180, -164.25) * mm, "end": v(-180, -169.25) * mm});
            skArc(sketch, "E378", {"start": v(-180, -169.25) * mm, "mid": v(-179.85, -169.6) * mm, "end": v(-179.5, -169.75) * mm});
            skLineSegment(sketch, "E379", {"start": v(-179.5, -169.75) * mm, "end": v(46.13, -169.75) * mm});
            skArc(sketch, "E380", {"start": v(46.13, -169.75) * mm, "mid": v(46.38, -169.69) * mm, "end": v(46.57, -169.5) * mm});
            skCircle(sketch, "E381", {"center": v(-16, -156.15) * mm, "radius": 1.6 * mm});
            skCircle(sketch, "E382", {"center": v(54, -19.15) * mm, "radius": 1.55 * mm});
            skCircle(sketch, "E383", {"center": v(54, 83.85) * mm, "radius": 1.55 * mm});
            skLineSegment(sketch, "E384", {"start": v(58, 147.85) * mm, "end": v(78, 147.85) * mm});
            skArc(sketch, "E385", {"start": v(58, 155.85) * mm, "mid": v(54, 151.85) * mm, "end": v(58, 147.85) * mm});
            skLineSegment(sketch, "E386", {"start": v(78, 155.85) * mm, "end": v(58, 155.85) * mm});
            skArc(sketch, "E387", {"start": v(78, 147.85) * mm, "mid": v(82, 151.85) * mm, "end": v(78, 155.85) * mm});
            skCircle(sketch, "E388", {"center": v(120, -123.15) * mm, "radius": 1.55 * mm});
            skCircle(sketch, "E389", {"center": v(150, -123.15) * mm, "radius": 1.55 * mm});
            skCircle(sketch, "E390", {"center": v(90, -123.15) * mm, "radius": 1.55 * mm});
            skLineSegment(sketch, "E391", {"start": v(155, -165.15) * mm, "end": v(142, -165.15) * mm});
            skArc(sketch, "E392", {"start": v(155, -173.15) * mm, "mid": v(159, -169.15) * mm, "end": v(155, -165.15) * mm});
            skLineSegment(sketch, "E393", {"start": v(142, -173.15) * mm, "end": v(155, -173.15) * mm});
            skArc(sketch, "E394", {"start": v(142, -165.15) * mm, "mid": v(138, -169.15) * mm, "end": v(142, -173.15) * mm});
            skLineSegment(sketch, "E395", {"start": v(109.5, -156.94) * mm, "end": v(109.5, -155.37) * mm});
            skArc(sketch, "E396", {"start": v(109.5, -156.94) * mm, "mid": v(109.57, -157.19) * mm, "end": v(109.75, -157.37) * mm});
            skArc(sketch, "E397", {"start": v(109.07, -158.05) * mm, "mid": v(109.85, -158.16) * mm, "end": v(109.75, -157.37) * mm});
            skArc(sketch, "E398", {"start": v(109.07, -158.05) * mm, "mid": v(108.88, -157.87) * mm, "end": v(108.63, -157.8) * mm});
            skLineSegment(sketch, "E399", {"start": v(104.17, -157.8) * mm, "end": v(108.63, -157.8) * mm});
            skArc(sketch, "E400", {"start": v(104.17, -157.8) * mm, "mid": v(103.92, -157.87) * mm, "end": v(103.73, -158.05) * mm});
            skArc(sketch, "E401", {"start": v(103.05, -157.37) * mm, "mid": v(102.95, -158.16) * mm, "end": v(103.73, -158.05) * mm});
            skArc(sketch, "E402", {"start": v(103.05, -157.37) * mm, "mid": v(103.23, -157.19) * mm, "end": v(103.3, -156.94) * mm});
            skLineSegment(sketch, "E403", {"start": v(103.3, -155.37) * mm, "end": v(103.3, -156.94) * mm});
            skArc(sketch, "E404", {"start": v(103.3, -155.37) * mm, "mid": v(103.23, -155.12) * mm, "end": v(103.05, -154.94) * mm});
            skArc(sketch, "E405", {"start": v(103.73, -154.25) * mm, "mid": v(102.95, -154.15) * mm, "end": v(103.05, -154.94) * mm});
            skArc(sketch, "E406", {"start": v(103.73, -154.25) * mm, "mid": v(103.92, -154.44) * mm, "end": v(104.17, -154.5) * mm});
            skLineSegment(sketch, "E407", {"start": v(108.63, -154.5) * mm, "end": v(104.17, -154.5) * mm});
            skArc(sketch, "E408", {"start": v(108.63, -154.5) * mm, "mid": v(108.88, -154.44) * mm, "end": v(109.07, -154.25) * mm});
            skArc(sketch, "E409", {"start": v(109.75, -154.94) * mm, "mid": v(109.85, -154.15) * mm, "end": v(109.07, -154.25) * mm});
            skArc(sketch, "E410", {"start": v(109.75, -154.94) * mm, "mid": v(109.57, -155.12) * mm, "end": v(109.5, -155.37) * mm});
            skLineSegment(sketch, "E411", {"start": v(130.7, -156.94) * mm, "end": v(130.7, -155.37) * mm});
            skArc(sketch, "E412", {"start": v(130.7, -156.94) * mm, "mid": v(130.77, -157.19) * mm, "end": v(130.95, -157.37) * mm});
            skArc(sketch, "E413", {"start": v(130.27, -158.05) * mm, "mid": v(131.05, -158.16) * mm, "end": v(130.95, -157.37) * mm});
            skArc(sketch, "E414", {"start": v(130.27, -158.05) * mm, "mid": v(130.08, -157.87) * mm, "end": v(129.83, -157.8) * mm});
            skLineSegment(sketch, "E415", {"start": v(125.37, -157.8) * mm, "end": v(129.83, -157.8) * mm});
            skArc(sketch, "E416", {"start": v(125.37, -157.8) * mm, "mid": v(125.12, -157.87) * mm, "end": v(124.93, -158.05) * mm});
            skArc(sketch, "E417", {"start": v(124.25, -157.37) * mm, "mid": v(124.15, -158.16) * mm, "end": v(124.93, -158.05) * mm});
            skArc(sketch, "E418", {"start": v(124.25, -157.37) * mm, "mid": v(124.43, -157.19) * mm, "end": v(124.5, -156.94) * mm});
            skLineSegment(sketch, "E419", {"start": v(124.5, -155.37) * mm, "end": v(124.5, -156.94) * mm});
            skArc(sketch, "E420", {"start": v(124.5, -155.37) * mm, "mid": v(124.43, -155.12) * mm, "end": v(124.25, -154.94) * mm});
            skArc(sketch, "E421", {"start": v(124.93, -154.25) * mm, "mid": v(124.15, -154.15) * mm, "end": v(124.25, -154.94) * mm});
            skArc(sketch, "E422", {"start": v(124.93, -154.25) * mm, "mid": v(125.12, -154.44) * mm, "end": v(125.37, -154.5) * mm});
            skLineSegment(sketch, "E423", {"start": v(129.83, -154.5) * mm, "end": v(125.37, -154.5) * mm});
            skArc(sketch, "E424", {"start": v(129.83, -154.5) * mm, "mid": v(130.08, -154.44) * mm, "end": v(130.27, -154.25) * mm});
            skArc(sketch, "E425", {"start": v(130.95, -154.94) * mm, "mid": v(131.05, -154.15) * mm, "end": v(130.27, -154.25) * mm});
            skArc(sketch, "E426", {"start": v(130.95, -154.94) * mm, "mid": v(130.77, -155.12) * mm, "end": v(130.7, -155.37) * mm});
            skCircle(sketch, "E427", {"center": v(152, -141.15) * mm, "radius": 1.6 * mm});
            skLineSegment(sketch, "E428", {"start": v(142.2, 41.85) * mm, "end": v(142.2, 121.85) * mm});
            skArc(sketch, "E429", {"start": v(137.8, 41.85) * mm, "mid": v(140, 39.65) * mm, "end": v(142.2, 41.85) * mm});
            skLineSegment(sketch, "E430", {"start": v(137.8, 121.85) * mm, "end": v(137.8, 41.85) * mm});
            skArc(sketch, "E431", {"start": v(142.2, 121.85) * mm, "mid": v(140, 124.05) * mm, "end": v(137.8, 121.85) * mm});
            skLineSegment(sketch, "E432", {"start": v(92.2, 41.85) * mm, "end": v(92.2, 121.85) * mm});
            skArc(sketch, "E433", {"start": v(87.8, 41.85) * mm, "mid": v(90, 39.65) * mm, "end": v(92.2, 41.85) * mm});
            skLineSegment(sketch, "E434", {"start": v(87.8, 121.85) * mm, "end": v(87.8, 41.85) * mm});
            skArc(sketch, "E435", {"start": v(92.2, 121.85) * mm, "mid": v(90, 124.05) * mm, "end": v(87.8, 121.85) * mm});
            skLineSegment(sketch, "E436", {"start": v(151, 18.85) * mm, "end": v(163, 18.85) * mm});
            skArc(sketch, "E437", {"start": v(147, 22.85) * mm, "mid": v(148.17, 20.02) * mm, "end": v(151, 18.85) * mm});
            skLineSegment(sketch, "E438", {"start": v(147, 114.85) * mm, "end": v(147, 22.85) * mm});
            skArc(sketch, "E439", {"start": v(151, 118.85) * mm, "mid": v(148.17, 117.68) * mm, "end": v(147, 114.85) * mm});
            skLineSegment(sketch, "E440", {"start": v(163, 118.85) * mm, "end": v(151, 118.85) * mm});
            skArc(sketch, "E441", {"start": v(167, 114.85) * mm, "mid": v(165.83, 117.68) * mm, "end": v(163, 118.85) * mm});
            skLineSegment(sketch, "E442", {"start": v(167, 22.85) * mm, "end": v(167, 114.85) * mm});
            skArc(sketch, "E443", {"start": v(163, 18.85) * mm, "mid": v(165.83, 20.02) * mm, "end": v(167, 22.85) * mm});
            skLineSegment(sketch, "E444", {"start": v(147, 0.85) * mm, "end": v(147, -91.15) * mm});
            skArc(sketch, "E445", {"start": v(151, 4.85) * mm, "mid": v(148.17, 3.68) * mm, "end": v(147, 0.85) * mm});
            skLineSegment(sketch, "E446", {"start": v(163, 4.85) * mm, "end": v(151, 4.85) * mm});
            skArc(sketch, "E447", {"start": v(167, 0.85) * mm, "mid": v(165.83, 3.68) * mm, "end": v(163, 4.85) * mm});
            skLineSegment(sketch, "E448", {"start": v(167, -91.15) * mm, "end": v(167, 0.85) * mm});
            skArc(sketch, "E449", {"start": v(163, -95.15) * mm, "mid": v(165.83, -93.98) * mm, "end": v(167, -91.15) * mm});
            skLineSegment(sketch, "E450", {"start": v(151, -95.15) * mm, "end": v(163, -95.15) * mm});
            skArc(sketch, "E451", {"start": v(147, -91.15) * mm, "mid": v(148.17, -93.98) * mm, "end": v(151, -95.15) * mm});
            skLineSegment(sketch, "E452", {"start": v(83, 22.85) * mm, "end": v(83, 114.85) * mm});
            skArc(sketch, "E453", {"start": v(79, 18.85) * mm, "mid": v(81.83, 20.02) * mm, "end": v(83, 22.85) * mm});
            skLineSegment(sketch, "E454", {"start": v(67, 18.85) * mm, "end": v(79, 18.85) * mm});
            skArc(sketch, "E455", {"start": v(63, 22.85) * mm, "mid": v(64.17, 20.02) * mm, "end": v(67, 18.85) * mm});
            skLineSegment(sketch, "E456", {"start": v(63, 114.85) * mm, "end": v(63, 22.85) * mm});
            skArc(sketch, "E457", {"start": v(67, 118.85) * mm, "mid": v(64.17, 117.68) * mm, "end": v(63, 114.85) * mm});
            skLineSegment(sketch, "E458", {"start": v(79, 118.85) * mm, "end": v(67, 118.85) * mm});
            skArc(sketch, "E459", {"start": v(83, 114.85) * mm, "mid": v(81.83, 117.68) * mm, "end": v(79, 118.85) * mm});
            skLineSegment(sketch, "E460", {"start": v(79, 4.85) * mm, "end": v(67, 4.85) * mm});
            skArc(sketch, "E461", {"start": v(83, 0.85) * mm, "mid": v(81.83, 3.68) * mm, "end": v(79, 4.85) * mm});
            skLineSegment(sketch, "E462", {"start": v(83, -91.15) * mm, "end": v(83, 0.85) * mm});
            skArc(sketch, "E463", {"start": v(79, -95.15) * mm, "mid": v(81.83, -93.98) * mm, "end": v(83, -91.15) * mm});
            skLineSegment(sketch, "E464", {"start": v(67, -95.15) * mm, "end": v(79, -95.15) * mm});
            skArc(sketch, "E465", {"start": v(63, -91.15) * mm, "mid": v(64.17, -93.98) * mm, "end": v(67, -95.15) * mm});
            skLineSegment(sketch, "E466", {"start": v(63, 0.85) * mm, "end": v(63, -91.15) * mm});
            skArc(sketch, "E467", {"start": v(67, 4.85) * mm, "mid": v(64.17, 3.68) * mm, "end": v(63, 0.85) * mm});
            skLineSegment(sketch, "E468", {"start": v(133, 22.85) * mm, "end": v(133, 114.85) * mm});
            skArc(sketch, "E469", {"start": v(129, 18.85) * mm, "mid": v(131.83, 20.02) * mm, "end": v(133, 22.85) * mm});
            skLineSegment(sketch, "E470", {"start": v(101, 18.85) * mm, "end": v(129, 18.85) * mm});
            skArc(sketch, "E471", {"start": v(97, 22.85) * mm, "mid": v(98.17, 20.02) * mm, "end": v(101, 18.85) * mm});
            skLineSegment(sketch, "E472", {"start": v(97, 114.85) * mm, "end": v(97, 22.85) * mm});
            skArc(sketch, "E473", {"start": v(101, 118.85) * mm, "mid": v(98.17, 117.68) * mm, "end": v(97, 114.85) * mm});
            skLineSegment(sketch, "E474", {"start": v(129, 118.85) * mm, "end": v(101, 118.85) * mm});
            skArc(sketch, "E475", {"start": v(133, 114.85) * mm, "mid": v(131.83, 117.68) * mm, "end": v(129, 118.85) * mm});
            skLineSegment(sketch, "E476", {"start": v(129, 4.85) * mm, "end": v(101, 4.85) * mm});
            skArc(sketch, "E477", {"start": v(133, 0.85) * mm, "mid": v(131.83, 3.68) * mm, "end": v(129, 4.85) * mm});
            skLineSegment(sketch, "E478", {"start": v(133, -91.15) * mm, "end": v(133, 0.85) * mm});
            skArc(sketch, "E479", {"start": v(129, -95.15) * mm, "mid": v(131.83, -93.98) * mm, "end": v(133, -91.15) * mm});
            skLineSegment(sketch, "E480", {"start": v(101, -95.15) * mm, "end": v(129, -95.15) * mm});
            skArc(sketch, "E481", {"start": v(97, -91.15) * mm, "mid": v(98.17, -93.98) * mm, "end": v(101, -95.15) * mm});
            skLineSegment(sketch, "E482", {"start": v(97, 0.85) * mm, "end": v(97, -91.15) * mm});
            skArc(sketch, "E483", {"start": v(101, 4.85) * mm, "mid": v(98.17, 3.68) * mm, "end": v(97, 0.85) * mm});
            skCircle(sketch, "E484", {"center": v(67, 141.85) * mm, "radius": 1.55 * mm});
            skCircle(sketch, "E485", {"center": v(90, 141.85) * mm, "radius": 1.55 * mm});
            skCircle(sketch, "E486", {"center": v(120, 141.85) * mm, "radius": 1.55 * mm});
            skCircle(sketch, "E487", {"center": v(150, 141.85) * mm, "radius": 1.55 * mm});
            skCircle(sketch, "E488", {"center": v(-117, -156.15) * mm, "radius": 1.6 * mm});
            skCircle(sketch, "E489", {"center": v(-103.25, -165.45) * mm, "radius": 1.55 * mm});
            skCircle(sketch, "E490", {"center": v(-29.25, -165.45) * mm, "radius": 1.55 * mm});
            skCircle(sketch, "E491", {"center": v(-163.25, -146.86) * mm, "radius": 1.55 * mm});
            skCircle(sketch, "E492", {"center": v(-29.25, -146.86) * mm, "radius": 1.55 * mm});
            skSolve(sketch);
        }
        {
            var Q0;
            Q0 = qSketchRegion(id + "F0", true);
            extrude(context, id + "F1", {"entities" : qUnion([Q0]), "depth" : 3 * mm, "offsetDistance" : 25 * mm});
        }
    });
